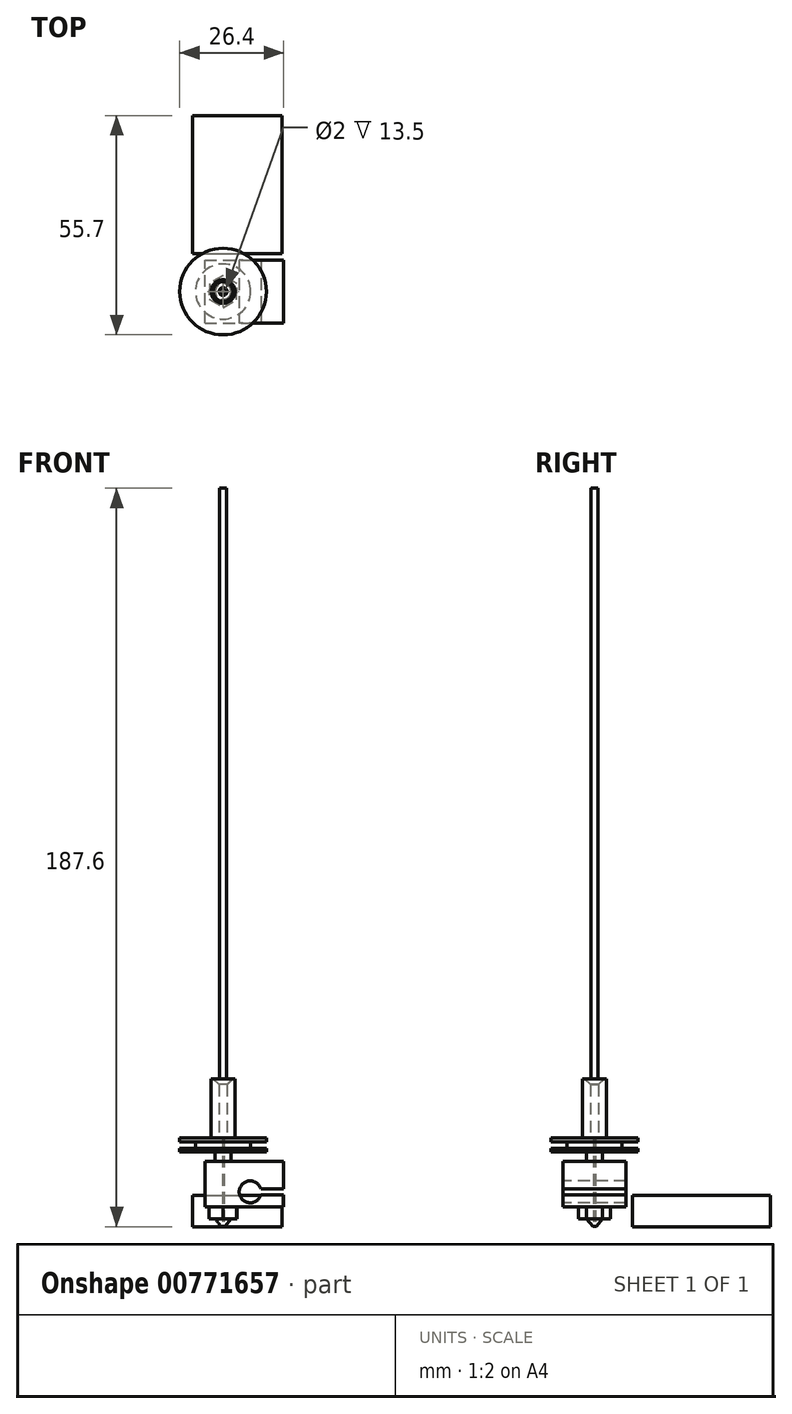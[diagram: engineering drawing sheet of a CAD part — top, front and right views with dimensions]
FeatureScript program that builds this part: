
annotation { "Feature Type Name" : "Feature", "Feature Type Description" : "" }
export const myFeature = defineFeature(function(context is Context, id is Id, definition is map)
    precondition{}
    {
        {
            var Q0;
            Q0=qCreatedBy(makeId("Top.planeOp"),FACE);
            var sketch = newSketch(context, id + "F0", { "sketchPlane" : qUnion([Q0])});
            skCircle(sketch, "E0", {"center": v(0, 0) * mm, "radius": 11 * mm});
            skSolve(sketch);
        }
        {
            var Q0;
            Q0=makeQuery(id+"F0.imprint","IMPRINT",FACE,{"disambiguationData":[TD([[makeQuery(id+"F0.imprint","IMPRINT",EDGE,{"derivedFrom":sQuery(id+"F0.wireOp",EDGE,"E0")}),1.0]])]});
            extrude(context, id + "F1", {"entities" : qUnion([Q0]), "oppositeDirection" : true, "depth" : 1 * mm, "offsetDistance" : 25 * mm});
        }
        {
            var Q0;
            Q0=makeQuery(id+"F1.opExtrude","CAP_FACE",FACE,{"disambiguationData":[OSD([sQuery(id+"F0.wireOp",EDGE,"E0")])],"isStart":false});
            var sketch = newSketch(context, id + "F2", { "sketchPlane" : qUnion([Q0])});
            skCircle(sketch, "E1", {"center": v(0, 0) * mm, "radius": 7 * mm});
            skSolve(sketch);
        }
        {
            var Q0;
            Q0=makeQuery(id+"F2.imprint","IMPRINT",FACE,{"disambiguationData":[TD([[makeQuery(id+"F2.imprint","IMPRINT",EDGE,{"derivedFrom":sQuery(id+"F2.wireOp",EDGE,"E1")}),1.0]])]});
            extrude(context, id + "F3", {"entities" : qUnion([Q0]), "operationType" : NewBodyOperationType.ADD, "depth" : 1.76 * mm, "offsetDistance" : 25 * mm});
        }
        {
            var Q0;
            Q0=makeQuery(id+"F3.opExtrude","CAP_FACE",FACE,{"disambiguationData":[OSD([sQuery(id+"F2.wireOp",EDGE,"E1")])],"isStart":false});
            var sketch = newSketch(context, id + "F4", { "sketchPlane" : qUnion([Q0])});
            skCircle(sketch, "E2", {"center": v(0, 0) * mm, "radius": 11 * mm});
            skSolve(sketch);
        }
        {
            var Q0;
            Q0 = qSketchRegion(id + "F4", true);
            extrude(context, id + "F5", {"entities" : qUnion([Q0]), "operationType" : NewBodyOperationType.ADD, "depth" : 0.9 * mm, "offsetDistance" : 25 * mm});
        }
        {
            var Q0;
            Q0=makeQuery(id+"F5.opExtrude","CAP_FACE",FACE,{"disambiguationData":[OSD([sQuery(id+"F4.wireOp",EDGE,"E2")])],"isStart":false});
            var sketch = newSketch(context, id + "F6", { "sketchPlane" : qUnion([Q0])});
            skCircle(sketch, "E3", {"center": v(0, 0) * mm, "radius": 2 * mm});
            skSolve(sketch);
        }
        {
            var Q0;
            Q0 = qSketchRegion(id + "F6", true);
            extrude(context, id + "F7", {"entities" : qUnion([Q0]), "operationType" : NewBodyOperationType.ADD, "depth" : 2.4 * mm, "offsetDistance" : 25 * mm});
        }
        {
            var Q0;
            Q0=makeQuery(id+"F7.opExtrude","CAP_FACE",FACE,{"disambiguationData":[OSD([sQuery(id+"F6.wireOp",EDGE,"E3")])],"isStart":false});
            var sketch = newSketch(context, id + "F8", { "sketchPlane" : qUnion([Q0])});
            skLineSegment(sketch, "E4.bottom", {"start": v(-4.6, 8) * mm, "end": v(15.4, 8) * mm});
            skLineSegment(sketch, "E4.top", {"start": v(-4.6, -8) * mm, "end": v(15.4, -8) * mm});
            skLineSegment(sketch, "E4.left", {"start": v(-4.6, 8) * mm, "end": v(-4.6, -8) * mm});
            skLineSegment(sketch, "E4.right", {"start": v(15.4, 8) * mm, "end": v(15.4, -8) * mm});
            skSolve(sketch);
        }
        {
            var Q0;
            Q0 = qSketchRegion(id + "F8", true);
            extrude(context, id + "F9", {"entities" : qUnion([Q0]), "operationType" : NewBodyOperationType.ADD, "depth" : 11.5 * mm, "offsetDistance" : 25 * mm});
        }
        {
            var Q0;
            Q0=makeQuery(id+"F9.opExtrude","SWEPT_FACE",FACE,{"disambiguationData":[OSD([sQuery(id+"F8.wireOp",EDGE,"E4.bottom")])]});
            var sketch = newSketch(context, id + "F10", { "sketchPlane" : qUnion([Q0])});
            skCircle(sketch, "E5", {"center": v(6.9, -13.76) * mm, "radius": 2.8 * mm});
            skSolve(sketch);
        }
        {
            var Q0;
            Q0 = qSketchRegion(id + "F10", true);
            extrude(context, id + "F11", {"entities" : qUnion([Q0]), "operationType" : NewBodyOperationType.REMOVE, "endBound" : BoundingType.THROUGH_ALL, "oppositeDirection" : true, "depth" : 25 * mm, "offsetDistance" : 25 * mm});
        }
        {
            var Q0;
            Q0=makeQuery(id+"F9.opExtrude","SWEPT_FACE",FACE,{"disambiguationData":[OSD([sQuery(id+"F8.wireOp",EDGE,"E4.right")])]});
            var sketch = newSketch(context, id + "F12", { "sketchPlane" : qUnion([Q0])});
            skLineSegment(sketch, "E6.bottom", {"start": v(-8, -13.06) * mm, "end": v(8, -13.06) * mm});
            skLineSegment(sketch, "E6.top", {"start": v(-8, -14.46) * mm, "end": v(8, -14.46) * mm});
            skLineSegment(sketch, "E6.left", {"start": v(-8, -13.06) * mm, "end": v(-8, -14.46) * mm});
            skLineSegment(sketch, "E6.right", {"start": v(8, -13.06) * mm, "end": v(8, -14.46) * mm});
            skSolve(sketch);
        }
        {
            var Q0;
            Q0 = qSketchRegion(id + "F12", true);
            extrude(context, id + "F13", {"entities" : qUnion([Q0]), "operationType" : NewBodyOperationType.REMOVE, "endBound" : BoundingType.UP_TO_NEXT, "oppositeDirection" : true, "depth" : 25 * mm, "offsetDistance" : 25 * mm});
        }
        {
            var Q0;
            Q0=makeQuery(id+"F9.opExtrude","CAP_FACE",FACE,{"disambiguationData":[OSD([sQuery(id+"F8.wireOp",EDGE,"E4.bottom"),sQuery(id+"F8.wireOp",EDGE,"E4.top"),sQuery(id+"F8.wireOp",EDGE,"E4.left"),sQuery(id+"F8.wireOp",EDGE,"E4.right")])],"isStart":false});
            var sketch = newSketch(context, id + "F14", { "sketchPlane" : qUnion([Q0])});
            skCircle(sketch, "E7.cCircle", {"center": v(0, 0) * mm, "radius": 4.04 * mm, "construction": true});
            skLineSegment(sketch, "E7.0", {"start": v(3.52, -1.98) * mm, "end": v(0.04, -4.04) * mm});
            skLineSegment(sketch, "E7.1", {"start": v(0.04, -4.04) * mm, "end": v(-3.48, -2.06) * mm});
            skLineSegment(sketch, "E7.2", {"start": v(-3.48, -2.06) * mm, "end": v(-3.52, 1.98) * mm});
            skLineSegment(sketch, "E7.3", {"start": v(-3.52, 1.98) * mm, "end": v(-0.04, 4.04) * mm});
            skLineSegment(sketch, "E7.4", {"start": v(-0.04, 4.04) * mm, "end": v(3.48, 2.06) * mm});
            skLineSegment(sketch, "E7.5", {"start": v(3.48, 2.06) * mm, "end": v(3.52, -1.98) * mm});
            skSolve(sketch);
        }
        {
            var Q0;
            Q0 = qSketchRegion(id + "F14", true);
            extrude(context, id + "F15", {"entities" : qUnion([Q0]), "operationType" : NewBodyOperationType.ADD, "depth" : 3 * mm, "offsetDistance" : 25 * mm});
        }
        {
            var Q0;
            Q0=makeQuery(id+"F15.opExtrude","CAP_FACE",FACE,{"disambiguationData":[OSD([sQuery(id+"F14.wireOp",EDGE,"E7.0"),sQuery(id+"F14.wireOp",EDGE,"E7.1"),sQuery(id+"F14.wireOp",EDGE,"E7.2"),sQuery(id+"F14.wireOp",EDGE,"E7.3"),sQuery(id+"F14.wireOp",EDGE,"E7.4"),sQuery(id+"F14.wireOp",EDGE,"E7.5")])],"isStart":false});
            var sketch = newSketch(context, id + "F16", { "sketchPlane" : qUnion([Q0])});
            skCircle(sketch, "E8", {"center": v(0, 0) * mm, "radius": 2.25 * mm});
            skSolve(sketch);
        }
        {
            var Q0;
            Q0 = qSketchRegion(id + "F16", true);
            extrude(context, id + "F17", {"entities" : qUnion([Q0]), "operationType" : NewBodyOperationType.ADD, "depth" : 2 * mm, "offsetDistance" : 25 * mm});
        }
        {
            var Q0;
            Q0=makeQuery(id+"F17.opExtrude","CAP_EDGE",EDGE,{"disambiguationData":[OSD([sQuery(id+"F16.wireOp",EDGE,"E8")])],"isStart":false});
            chamfer(context, id + "F18", {"entities" : qUnion([Q0]), "chamferType" : ChamferType.TWO_OFFSETS, "width1" : 1.8 * mm, "oppositeDirection" : false, "width2" : 2.2 * mm, "tangentPropagation" : true});
        }
        {
            var Q0;
            Q0=makeQuery(id+"F1.opExtrude","CAP_FACE",FACE,{"disambiguationData":[OSD([sQuery(id+"F0.wireOp",EDGE,"E0")])],"isStart":true});
            var sketch = newSketch(context, id + "F19", { "sketchPlane" : qUnion([Q0])});
            skCircle(sketch, "E9", {"center": v(0, 0) * mm, "radius": 3 * mm});
            skSolve(sketch);
        }
        {
            var Q0;
            Q0 = qSketchRegion(id + "F19", true);
            extrude(context, id + "F20", {"entities" : qUnion([Q0]), "operationType" : NewBodyOperationType.ADD, "depth" : 15 * mm, "offsetDistance" : 25 * mm});
        }
        {
            var Q0;
            Q0=makeQuery(id+"F17.opExtrude","CAP_FACE",FACE,{"disambiguationData":[OSD([sQuery(id+"F16.wireOp",EDGE,"E8")])],"isStart":false});
            var sketch = newSketch(context, id + "F21", { "sketchPlane" : qUnion([Q0])});
            skCircle(sketch, "E10", {"center": v(0, 0) * mm, "radius": 0.2 * mm});
            skSolve(sketch);
        }
        {
            var Q0;
            Q0 = qSketchRegion(id + "F21", true);
            extrude(context, id + "F22", {"entities" : qUnion([Q0]), "operationType" : NewBodyOperationType.REMOVE, "endBound" : BoundingType.THROUGH_ALL, "oppositeDirection" : true, "depth" : 25 * mm, "offsetDistance" : 25 * mm});
        }
        {
            var Q0;
            Q0=makeQuery(id+"F1.opExtrude","CAP_FACE",FACE,{"disambiguationData":[OSD([sQuery(id+"F0.wireOp",EDGE,"E0")])],"isStart":true});
            var sketch = newSketch(context, id + "F23", { "sketchPlane" : qUnion([Q0])});
            skCircle(sketch, "E11", {"center": v(0, 0) * mm, "radius": 1 * mm});
            skSolve(sketch);
        }
        {
            var Q0;
            Q0 = qSketchRegion(id + "F23", true);
            extrude(context, id + "F24", {"entities" : qUnion([Q0]), "operationType" : NewBodyOperationType.REMOVE, "endBound" : BoundingType.THROUGH_ALL, "depth" : 20 * mm, "offsetDistance" : 25 * mm});
        }
        {
            var Q0;
            Q0=makeQuery(id+"F24.boolean.opBoolean","INTERSECT",EDGE,{"derivedFrom":[makeQuery(id+"F20.opExtrude","CAP_FACE",FACE,{"disambiguationData":[OSD([sQuery(id+"F19.wireOp",EDGE,"E9")])],"isStart":false}),makeQuery(id+"F24.opExtrude","SWEPT_FACE",FACE,{"disambiguationData":[OSD([sQuery(id+"F23.wireOp",EDGE,"E11")])]})]});
            chamfer(context, id + "F25", {"entities" : qUnion([Q0]), "width" : 1.5 * mm, "tangentPropagation" : true});
        }
        {
            var Q0;
            Q0=qCreatedBy(makeId("Top.planeOp"),FACE);
            cPlane(context, id + "F26", {"entities" : qUnion([Q0]), "cplaneType" : CPlaneType.OFFSET, "offset" : 22.6 * mm, "oppositeDirection" : true, "width" : 150 * mm, "height" : 150 * mm});
        }
        {
            var Q0;
            Q0=qCreatedBy(id+"F26.planeOp",FACE);
            var sketch = newSketch(context, id + "F27", { "sketchPlane" : qUnion([Q0])});
            skLineSegment(sketch, "E12.bottom", {"start": v(-7.8, 44.7) * mm, "end": v(14.92, 44.7) * mm});
            skLineSegment(sketch, "E12.top", {"start": v(-7.8, 9.65) * mm, "end": v(14.92, 9.65) * mm});
            skLineSegment(sketch, "E12.left", {"start": v(-7.8, 44.7) * mm, "end": v(-7.8, 9.65) * mm});
            skLineSegment(sketch, "E12.right", {"start": v(14.92, 44.7) * mm, "end": v(14.92, 9.65) * mm});
            skSolve(sketch);
        }
        {
            var Q0;
            Q0 = qSketchRegion(id + "F27", true);
            extrude(context, id + "F28", {"entities" : qUnion([Q0]), "depth" : 8 * mm, "offsetDistance" : 25 * mm});
        }
        {
            var Q0;
            Q0=qCreatedBy(makeId("Top.planeOp"),FACE);
            cPlane(context, id + "F29", {"entities" : qUnion([Q0]), "cplaneType" : CPlaneType.OFFSET, "offset" : 15 * mm, "width" : 150 * mm, "height" : 150 * mm});
        }
        {
            var Q0;
            Q0=qCreatedBy(id+"F29.planeOp",FACE);
            var sketch = newSketch(context, id + "F30", { "sketchPlane" : qUnion([Q0])});
            skCircle(sketch, "E13", {"center": v(0, 0) * mm, "radius": 0.88 * mm});
            skSolve(sketch);
        }
        {
            var Q0;
            Q0 = qSketchRegion(id + "F30", true);
            extrude(context, id + "F31", {"entities" : qUnion([Q0]), "depth" : 150 * mm, "offsetDistance" : 25 * mm});
        }
    });
